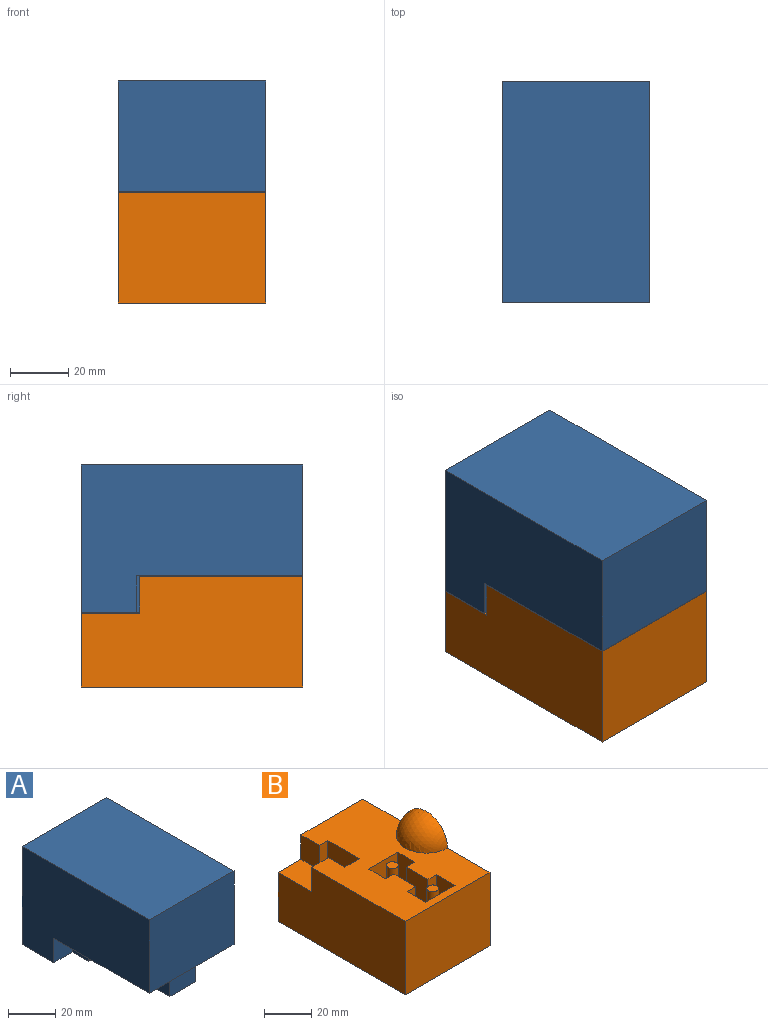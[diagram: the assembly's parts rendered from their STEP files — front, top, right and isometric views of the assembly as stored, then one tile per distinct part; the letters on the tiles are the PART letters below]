
ASSEMBLY  parts=2 mates=1
PART A: 31 faces, bbox 50.8x76.2x50.8 mm
  f0: plane 50.8x50.8mm, normal (0,1,0), area 2096.8mm2, adj f1,f3,f4,f5,f25,f30
  f1: plane 76.2x50.8mm, normal (-1,0,0), area 3145.2mm2, adj f0,f2,f4,f5,f26,f30
  f2: plane 50.8x38.1mm, normal (0,-1,0), area 1935.5mm2, adj f1,f3,f4,f5
  f3: plane 76.2x38.1mm, normal (1,0,0), area 2607.7mm2, adj f0,f2,f4,f5,f23
  f4: plane 76.2x50.8mm, normal (0,0,1), area 3871mm2, adj f0,f1,f2,f3
  f5: plane 76.2x50.8mm, normal (0,0,-1), area 2885.8mm2, adj f0,f1,f2,f3,f6,f7,f8,f9
  f6: plane 12.7x5.08mm, normal (0,-1,0), area 64.5mm2, adj f5,f7,f17,f20
  f7: plane 14.99x12.7mm, normal (-1,0,0), area 190.3mm2, adj f5,f6,f8,f20
  f8: plane 12.7x5.08mm, normal (0,1,0), area 64.5mm2, adj f5,f7,f9,f20
  f9: plane 12.7x9.14mm, normal (-1,0,0), area 116.1mm2, adj f5,f8,f10,f20
  f10: plane 15.49x12.7mm, normal (0,-1,0), area 196.8mm2, adj f5,f9,f11,f20
  f11: plane 12.7x9.14mm, normal (1,0,0), area 116.1mm2, adj f5,f10,f12,f20
  f12: plane 12.7x5.08mm, normal (0,1,0), area 64.5mm2, adj f5,f11,f13,f20
  f13: plane 14.99x12.7mm, normal (1,0,0), area 190.3mm2, adj f5,f12,f14,f20
  f14: plane 12.7x5.08mm, normal (0,-1,0), area 64.5mm2, adj f5,f13,f15,f20
  f15: plane 12.7x8.13mm, normal (1,0,0), area 103.2mm2, adj f5,f14,f16,f20
  f16: plane 15.49x12.7mm, normal (0,1,0), area 196.8mm2, adj f5,f15,f17,f20
  f17: plane 12.7x8.13mm, normal (-1,0,0), area 103.2mm2, adj f5,f6,f16,f20
  f18: cylinder r=3.05mm len=12.7mm, axis (0,0,1), area 243.2mm2, adj f20,f22
  f19: cylinder r=3.05mm len=12.7mm, axis (0,0,1), area 243.2mm2, adj f20,f21
  f20: plane 32.26x15.49mm, normal (0,0,-1), area 289.2mm2, adj f6,f7,f8,f9,f10,f11,f12,f13
  f21: plane 6.1x6.1mm, normal (0,0,-1), area 29.2mm2, adj f19
  f22: plane 6.1x6.1mm, normal (0,0,-1), area 29.2mm2, adj f18
  f23: sphere r=13.72mm, area 591mm2, adj f3,f5
  f24: plane 12.7x5.08mm, normal (0,1,0), area 64.5mm2, adj f5,f25,f29,f30
  f25: plane 12.7x12.14mm, normal (1,0,0), area 154.2mm2, adj f0,f5,f24,f30
  f26: plane 12.7x11.18mm, normal (0,-1,0), area 141.9mm2, adj f1,f5,f27,f30
  f27: plane 12.7x9.86mm, normal (-1,0,0), area 125.2mm2, adj f5,f26,f28,f30
  f28: plane 12.7x6.6mm, normal (0,-1,0), area 83.9mm2, adj f5,f27,f29,f30
  f29: plane 16.76x12.7mm, normal (1,0,0), area 212.9mm2, adj f5,f24,f28,f30
  f30: plane 28.91x17.78mm, normal (0,0,-1), area 342.1mm2, adj f0,f1,f24,f25,f26,f27,f28,f29
PART B: 31 faces, bbox 50.8x76.2x50.8 mm
  f0: plane 76.2x38.1mm, normal (-1,0,0), area 2648.4mm2, adj f1,f2,f4,f5,f9,f13
  f1: plane 50.8x38.1mm, normal (0,1,0), area 1761.3mm2, adj f0,f3,f4,f5,f8,f13
  f2: plane 50.8x38.1mm, normal (0,-1,0), area 1935.5mm2, adj f0,f3,f4,f5
  f3: plane 76.2x50.8mm, normal (1,0,0), area 3156.6mm2, adj f1,f2,f4,f5,f6
  f4: plane 76.2x50.8mm, normal (0,0,1), area 2744.1mm2, adj f0,f1,f2,f3,f6,f7,f8,f9
  f5: plane 76.2x50.8mm, normal (0,0,-1), area 3871mm2, adj f0,f1,f2,f3
  f6: sphere r=12.7mm, area 506.7mm2, adj f3,f4
  f7: plane 12.7x5.08mm, normal (0,-1,0), area 64.5mm2, adj f4,f8,f12,f13
  f8: plane 12.7x11.12mm, normal (-1,0,0), area 141.3mm2, adj f1,f4,f7,f13
  f9: plane 12.7x10.16mm, normal (0,1,0), area 129mm2, adj f0,f4,f10,f13
  f10: plane 12.7x9.85mm, normal (1,0,0), area 125.1mm2, adj f4,f9,f11,f13
  f11: plane 12.7x8.64mm, normal (0,1,0), area 109.7mm2, adj f4,f10,f12,f13
  f12: plane 18.8x12.7mm, normal (-1,0,0), area 238.7mm2, adj f4,f7,f11,f13
  f13: plane 29.92x18.8mm, normal (0,0,1), area 405.7mm2, adj f0,f1,f7,f8,f9,f10,f11,f12
  f14: plane 12.7x5.08mm, normal (0,-1,0), area 64.5mm2, adj f4,f15,f27,f28
  f15: plane 12.7x11.18mm, normal (1,0,0), area 141.9mm2, adj f4,f14,f16,f28
  f16: plane 17.53x12.7mm, normal (0,1,0), area 222.6mm2, adj f4,f15,f17,f28
  f17: plane 12.7x11.18mm, normal (-1,0,0), area 141.9mm2, adj f4,f16,f18,f28
  f18: plane 12.7x5.08mm, normal (0,-1,0), area 64.5mm2, adj f4,f17,f19,f28
  f19: plane 12.95x12.7mm, normal (-1,0,0), area 164.5mm2, adj f4,f18,f20,f28
  f20: plane 12.7x5.08mm, normal (0,1,0), area 64.5mm2, adj f4,f19,f21,f28
  f21: plane 12.7x10.16mm, normal (-1,0,0), area 129mm2, adj f4,f20,f22,f28
  f22: plane 17.37x12.7mm, normal (0,-1,0), area 220.6mm2, adj f4,f21,f23,f28
  f23: plane 12.7x10.16mm, normal (1,0,0), area 129mm2, adj f4,f22,f24,f28
  f24: plane 12.7x4.93mm, normal (0,1,0), area 62.6mm2, adj f4,f23,f27,f28
  f25: cylinder r=2.54mm len=12.7mm, axis (0,0,1), area 202.7mm2, adj f28,f29
  f26: cylinder r=2.54mm len=12.7mm, axis (0,0,1), area 202.7mm2, adj f28,f30
  f27: plane 12.95x12.7mm, normal (1,0,0), area 164.5mm2, adj f4,f14,f24,f28
  f28: plane 34.29x17.53mm, normal (0,0,1), area 427.3mm2, adj f14,f15,f16,f17,f18,f19,f20,f21
  f29: plane 5.08x5.08mm, normal (0,0,1), area 20.3mm2, adj f25
  f30: plane 5.08x5.08mm, normal (0,0,1), area 20.3mm2, adj f26
PLACE A t=(0,0,0.16)mm
PLACE B at identity fixed
MATE slider A.f30 <-> B.f13  axis (0,0,-1) through (-25.4,38.1,25.56)mm
